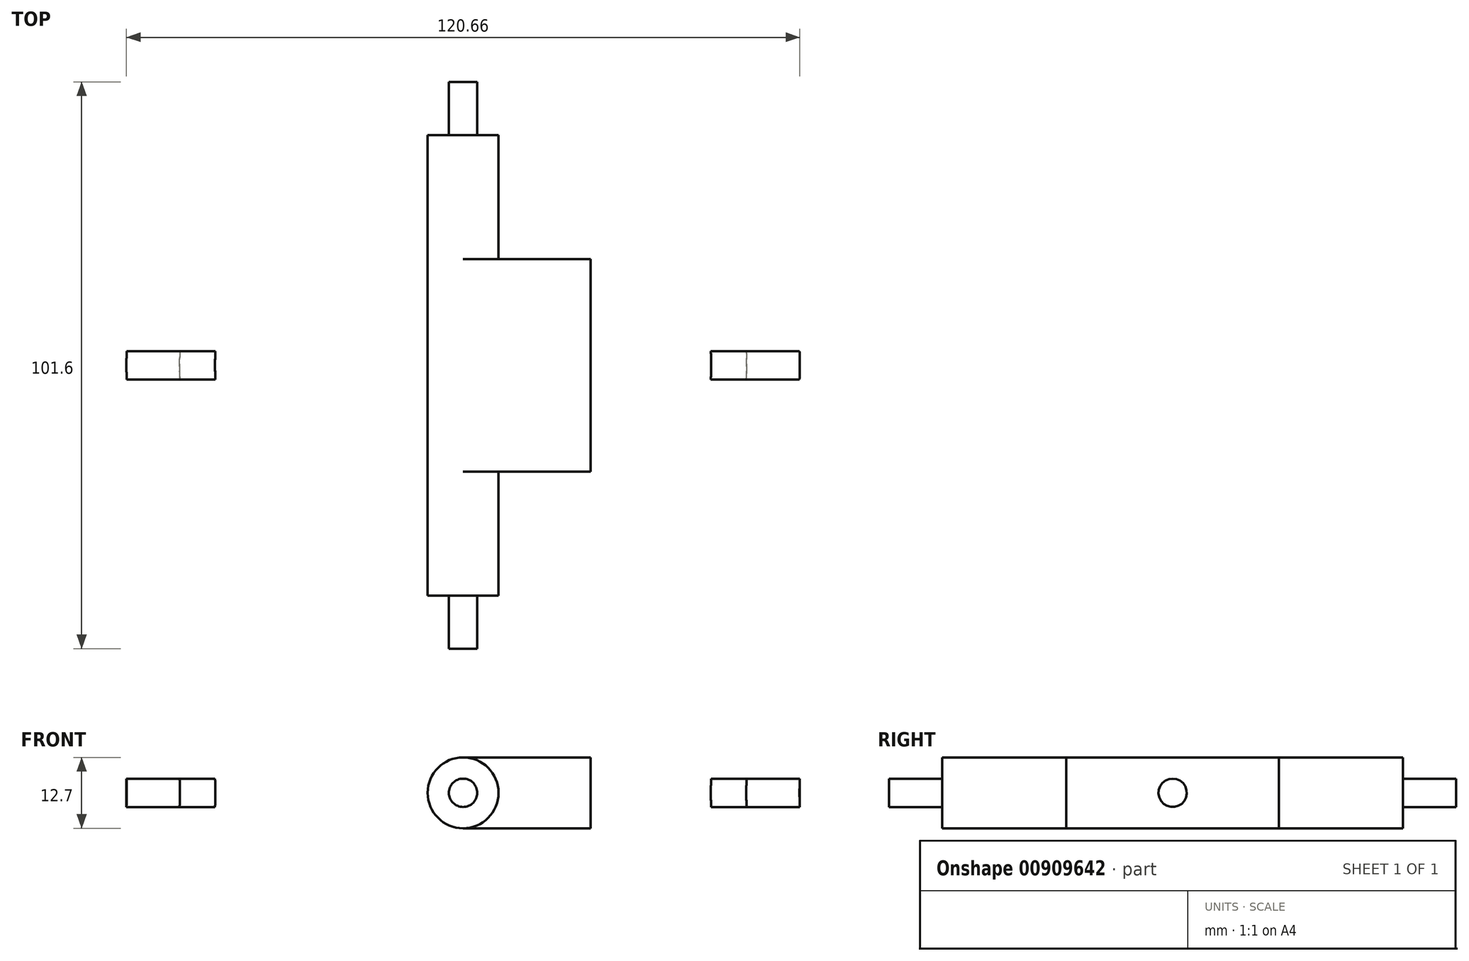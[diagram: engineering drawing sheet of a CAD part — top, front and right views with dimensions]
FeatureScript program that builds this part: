
annotation { "Feature Type Name" : "Feature", "Feature Type Description" : "" }
export const myFeature = defineFeature(function(context is Context, id is Id, definition is map)
    precondition{}
    {
        {
            var Q0;
            Q0=qCreatedBy(makeId("Top.planeOp"),FACE);
            var sketch = newSketch(context, id + "F0", { "sketchPlane" : qUnion([Q0])});
            skCircle(sketch, "E0", {"center": v(0, 0) * mm, "radius": 63.5 * mm});
            skCircle(sketch, "E1.0", {"center": v(0, 0) * mm, "radius": 69.85 * mm});
            skSolve(sketch);
        }
        {
            var Q0;
            Q0=makeQuery(id+"F0.imprint","IMPRINT",FACE,{"disambiguationData":[TD([[makeQuery(id+"F0.imprint","IMPRINT",EDGE,{"derivedFrom":sQuery(id+"F0.wireOp",EDGE,"E0")}),-1.0]])]});
            extrude(context, id + "F1", {"entities" : qUnion([Q0]), "depth" : 12.7 * mm, "offsetDistance" : 25.4 * mm});
        }
        {
            var Q0;
            Q0=qCreatedBy(makeId("Front.planeOp"),FACE);
            var sketch = newSketch(context, id + "F2", { "sketchPlane" : qUnion([Q0])});
            skCircle(sketch, "E2", {"center": v(0, 6.35) * mm, "radius": 2.54 * mm});
            skSolve(sketch);
        }
        {
            var Q0;
            Q0=sQuery(id+"F2.wireOp",VERTEX,"E2.center");
            var Q1;
            Q1=makeQuery(id+"F1.opExtrude","SWEPT_BODY",BODY,{"disambiguationData":[OSD([sQuery(id+"F0.wireOp",EDGE,"E0"),sQuery(id+"F0.wireOp",EDGE,"E1.0")])]});
            hole(context, id + "F3", {"style" : HoleStyle.SIMPLE, "endStyle" : HoleEndStyle.THROUGH, "holeDiameter" : 7.62 * mm, "majorDiameter" : 6.35 * mm, "isTappedThrough" : true, "tappedDepth" : 12.7 * mm, "tapClearance" : 3, "locations" : qUnion([Q0]), "scope" : qUnion([Q1])});
        }
        {
            var Q0;
            Q0=sQuery(id+"F2.wireOp",VERTEX,"E2.center");
            var Q1;
            Q1=makeQuery(id+"F1.opExtrude","SWEPT_BODY",BODY,{"disambiguationData":[OSD([sQuery(id+"F0.wireOp",EDGE,"E0"),sQuery(id+"F0.wireOp",EDGE,"E1.0")])]});
            hole(context, id + "F4", {"style" : HoleStyle.SIMPLE, "endStyle" : HoleEndStyle.THROUGH, "oppositeDirection" : true, "holeDiameter" : 7.62 * mm, "majorDiameter" : 6.35 * mm, "isTappedThrough" : true, "tappedDepth" : 12.7 * mm, "tapClearance" : 3, "locations" : qUnion([Q0]), "scope" : qUnion([Q1])});
        }
        {
            var Q0;
            Q0=qCreatedBy(makeId("Top.planeOp"),FACE);
            var sketch = newSketch(context, id + "F5", { "sketchPlane" : qUnion([Q0])});
            skCircle(sketch, "E3", {"center": v(0, 0) * mm, "radius": 53.98 * mm});
            skCircle(sketch, "E4.0", {"center": v(0, 0) * mm, "radius": 60.33 * mm});
            skSolve(sketch);
        }
        {
            var Q0;
            Q0=makeQuery(id+"F5.imprint","IMPRINT",FACE,{"disambiguationData":[TD([[makeQuery(id+"F5.imprint","IMPRINT",EDGE,{"derivedFrom":sQuery(id+"F5.wireOp",EDGE,"E4.0")}),1.0]])]});
            extrude(context, id + "F6", {"entities" : qUnion([Q0]), "depth" : 12.7 * mm, "offsetDistance" : 25.4 * mm});
        }
        {
            var Q0;
            Q0=qCreatedBy(makeId("Top.planeOp"),FACE);
            var sketch = newSketch(context, id + "F7", { "sketchPlane" : qUnion([Q0])});
            skCircle(sketch, "E5", {"center": v(0, 0) * mm, "radius": 53.98 * mm});
            skCircle(sketch, "E6.0", {"center": v(0, 0) * mm, "radius": 69.85 * mm});
            skSolve(sketch);
        }
        {
            var Q0;
            Q0=makeQuery(id+"F7.imprint","IMPRINT",FACE,{"disambiguationData":[TD([[makeQuery(id+"F7.imprint","IMPRINT",EDGE,{"derivedFrom":sQuery(id+"F7.wireOp",EDGE,"E5")}),-1.0]])]});
            extrude(context, id + "F8", {"entities" : qUnion([Q0]), "depth" : 12.7 * mm, "offsetDistance" : 25.4 * mm});
        }
        {
            var Q0;
            Q0=makeQuery(id+"F2.imprint","IMPRINT",FACE,{"disambiguationData":[TD([[makeQuery(id+"F2.imprint","IMPRINT",EDGE,{"derivedFrom":sQuery(id+"F2.wireOp",EDGE,"E2")}),1.0]])]});
            extrude(context, id + "F9", {"entities" : qUnion([Q0]), "operationType" : NewBodyOperationType.INTERSECT, "endBound" : BoundingType.SYMMETRIC, "depth" : 139.7 * mm, "offsetDistance" : 25.4 * mm});
        }
        {
            var Q0;
            Q0=qCreatedBy(makeId("Right.planeOp"),FACE);
            var sketch = newSketch(context, id + "F10", { "sketchPlane" : qUnion([Q0])});
            skCircle(sketch, "E7", {"center": v(0, 6.35) * mm, "radius": 2.54 * mm});
            skSolve(sketch);
        }
        {
            var Q0;
            Q0=sQuery(id+"F10.wireOp",VERTEX,"E7.center");
            var Q1;
            Q1=makeQuery(id+"F6.opExtrude","SWEPT_BODY",BODY,{"disambiguationData":[OSD([sQuery(id+"F5.wireOp",EDGE,"E4.0"),sQuery(id+"F5.wireOp",EDGE,"E3")])]});
            hole(context, id + "F11", {"style" : HoleStyle.SIMPLE, "endStyle" : HoleEndStyle.THROUGH, "holeDiameter" : 7.62 * mm, "majorDiameter" : 6.35 * mm, "isTappedThrough" : true, "tappedDepth" : 12.7 * mm, "tapClearance" : 3, "locations" : qUnion([Q0]), "scope" : qUnion([Q1])});
        }
        {
            var Q0;
            Q0=sQuery(id+"F10.wireOp",VERTEX,"E7.center");
            var Q1;
            Q1=makeQuery(id+"F6.opExtrude","SWEPT_BODY",BODY,{"disambiguationData":[OSD([sQuery(id+"F5.wireOp",EDGE,"E4.0"),sQuery(id+"F5.wireOp",EDGE,"E3")])]});
            hole(context, id + "F12", {"style" : HoleStyle.SIMPLE, "endStyle" : HoleEndStyle.THROUGH, "oppositeDirection" : true, "holeDiameter" : 7.62 * mm, "majorDiameter" : 6.35 * mm, "isTappedThrough" : true, "tappedDepth" : 12.7 * mm, "tapClearance" : 3, "locations" : qUnion([Q0]), "scope" : qUnion([Q1])});
        }
        {
            var Q0;
            Q0=qCreatedBy(makeId("Top.planeOp"),FACE);
            var sketch = newSketch(context, id + "F13", { "sketchPlane" : qUnion([Q0])});
            skCircle(sketch, "E8", {"center": v(0, 0) * mm, "radius": 44.45 * mm});
            skCircle(sketch, "E9.0", {"center": v(0, 0) * mm, "radius": 50.8 * mm});
            skSolve(sketch);
        }
        {
            var Q0;
            Q0=makeQuery(id+"F13.imprint","IMPRINT",FACE,{"disambiguationData":[TD([[makeQuery(id+"F13.imprint","IMPRINT",EDGE,{"derivedFrom":sQuery(id+"F13.wireOp",EDGE,"E8")}),-1.0]])]});
            extrude(context, id + "F14", {"entities" : qUnion([Q0]), "depth" : 12.7 * mm, "offsetDistance" : 25.4 * mm});
        }
        {
            var Q0;
            Q0=sQuery(id+"F2.wireOp",VERTEX,"E2.center");
            var Q1;
            Q1=makeQuery(id+"F14.opExtrude","SWEPT_BODY",BODY,{"disambiguationData":[OSD([sQuery(id+"F13.wireOp",EDGE,"E8"),sQuery(id+"F13.wireOp",EDGE,"E9.0")])]});
            hole(context, id + "F15", {"style" : HoleStyle.SIMPLE, "endStyle" : HoleEndStyle.THROUGH, "holeDiameter" : 7.62 * mm, "majorDiameter" : 6.35 * mm, "isTappedThrough" : true, "tappedDepth" : 12.7 * mm, "tapClearance" : 3, "locations" : qUnion([Q0]), "scope" : qUnion([Q1])});
        }
        {
            var Q0;
            Q0=sQuery(id+"F2.wireOp",VERTEX,"E2.center");
            var Q1;
            Q1=makeQuery(id+"F14.opExtrude","SWEPT_BODY",BODY,{"disambiguationData":[OSD([sQuery(id+"F13.wireOp",EDGE,"E8"),sQuery(id+"F13.wireOp",EDGE,"E9.0")])]});
            hole(context, id + "F16", {"style" : HoleStyle.SIMPLE, "endStyle" : HoleEndStyle.THROUGH, "oppositeDirection" : true, "holeDiameter" : 7.62 * mm, "majorDiameter" : 6.35 * mm, "isTappedThrough" : true, "tappedDepth" : 12.7 * mm, "tapClearance" : 3, "locations" : qUnion([Q0]), "scope" : qUnion([Q1])});
        }
        {
            var Q0;
            Q0=qCreatedBy(makeId("Top.planeOp"),FACE);
            var sketch = newSketch(context, id + "F17", { "sketchPlane" : qUnion([Q0])});
            skCircle(sketch, "E10", {"center": v(0, 0) * mm, "radius": 44.45 * mm});
            skCircle(sketch, "E11", {"center": v(0, 0) * mm, "radius": 60.33 * mm});
            skSolve(sketch);
        }
        {
            var Q0;
            Q0=makeQuery(id+"F17.imprint","IMPRINT",FACE,{"disambiguationData":[TD([[makeQuery(id+"F17.imprint","IMPRINT",EDGE,{"derivedFrom":sQuery(id+"F17.wireOp",EDGE,"E10")}),-1.0]])]});
            extrude(context, id + "F18", {"entities" : qUnion([Q0]), "depth" : 12.7 * mm, "offsetDistance" : 25.4 * mm});
        }
        {
            var Q0;
            Q0=makeQuery(id+"F10.imprint","IMPRINT",FACE,{"disambiguationData":[TD([[makeQuery(id+"F10.imprint","IMPRINT",EDGE,{"derivedFrom":sQuery(id+"F10.wireOp",EDGE,"E7")}),1.0]])]});
            extrude(context, id + "F19", {"entities" : qUnion([Q0]), "operationType" : NewBodyOperationType.INTERSECT, "endBound" : BoundingType.SYMMETRIC, "depth" : 127 * mm, "offsetDistance" : 25.4 * mm});
        }
        {
            var Q0;
            Q0=makeQuery(id+"F2.imprint","IMPRINT",FACE,{"disambiguationData":[TD([[makeQuery(id+"F2.imprint","IMPRINT",EDGE,{"derivedFrom":sQuery(id+"F2.wireOp",EDGE,"E2")}),1.0]])]});
            extrude(context, id + "F20", {"entities" : qUnion([Q0]), "endBound" : BoundingType.SYMMETRIC, "depth" : 101.6 * mm, "offsetDistance" : 25.4 * mm});
        }
        {
            var Q0;
            Q0=qCreatedBy(makeId("Front.planeOp"),FACE);
            var sketch = newSketch(context, id + "F21", { "sketchPlane" : qUnion([Q0])});
            skCircle(sketch, "E12", {"center": v(0, 6.35) * mm, "radius": 6.35 * mm});
            skSolve(sketch);
        }
        {
            var Q0;
            Q0=makeQuery(id+"F21.imprint","IMPRINT",FACE,{"disambiguationData":[TD([[makeQuery(id+"F21.imprint","IMPRINT",EDGE,{"derivedFrom":sQuery(id+"F21.wireOp",EDGE,"E12")}),1.0]])]});
            extrude(context, id + "F22", {"entities" : qUnion([Q0]), "operationType" : NewBodyOperationType.ADD, "endBound" : BoundingType.SYMMETRIC, "depth" : 82.55 * mm, "offsetDistance" : 25.4 * mm});
        }
        {
            var Q0;
            Q0=qCreatedBy(makeId("Top.planeOp"),FACE);
            var sketch = newSketch(context, id + "F23", { "sketchPlane" : qUnion([Q0])});
            skLineSegment(sketch, "E13.bottom", {"start": v(0, -19.05) * mm, "end": v(22.82, -19.05) * mm});
            skLineSegment(sketch, "E13.top", {"start": v(0, 19.05) * mm, "end": v(22.82, 19.05) * mm});
            skLineSegment(sketch, "E13.left", {"start": v(0, -19.05) * mm, "end": v(0, 19.05) * mm});
            skLineSegment(sketch, "E13.right", {"start": v(22.82, -19.05) * mm, "end": v(22.82, 19.05) * mm});
            skSolve(sketch);
        }
        {
            var Q0;
            Q0=makeQuery(id+"F23.imprint","IMPRINT",FACE,{"disambiguationData":[TD([[makeQuery(id+"F23.imprint","IMPRINT",EDGE,{"derivedFrom":sQuery(id+"F23.wireOp",EDGE,"E13.bottom")}),1.0]])]});
            extrude(context, id + "F24", {"entities" : qUnion([Q0]), "operationType" : NewBodyOperationType.ADD, "depth" : 12.7 * mm, "offsetDistance" : 25.4 * mm});
        }
    });
